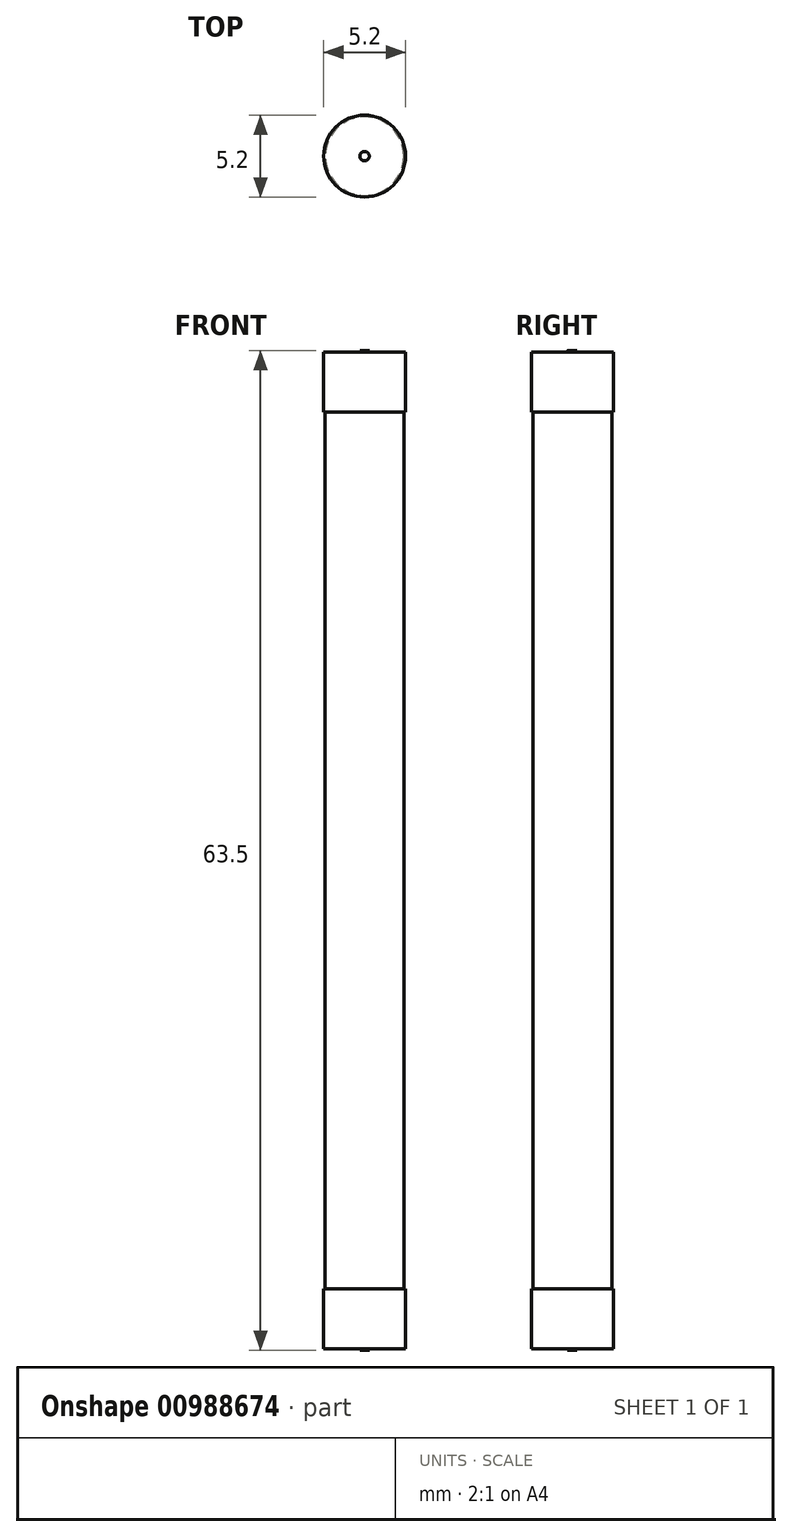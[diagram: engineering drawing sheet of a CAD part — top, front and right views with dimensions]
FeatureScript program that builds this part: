
annotation { "Feature Type Name" : "Feature", "Feature Type Description" : "" }
export const myFeature = defineFeature(function(context is Context, id is Id, definition is map)
    precondition{}
    {
        {
            var Q0;
            Q0=qCreatedBy(makeId("Top.planeOp"),FACE);
            var sketch = newSketch(context, id + "F0", { "sketchPlane" : qUnion([Q0])});
            skCircle(sketch, "E0", {"center": v(0, 0) * mm, "radius": 2.5 * mm});
            skSolve(sketch);
        }
        {
            var Q0;
            Q0=makeQuery(id+"F0.imprint","IMPRINT",FACE,{"disambiguationData":[TD([[makeQuery(id+"F0.imprint","IMPRINT",EDGE,{"derivedFrom":sQuery(id+"F0.wireOp",EDGE,"E0")}),1.0]])]});
            extrude(context, id + "F1", {"entities" : qUnion([Q0]), "endBound" : BoundingType.SYMMETRIC, "depth" : 55.67 * mm, "offsetDistance" : 25 * mm});
        }
        {
            var Q0;
            Q0=makeQuery(id+"F1.opExtrude","CAP_FACE",FACE,{"disambiguationData":[OSD([sQuery(id+"F0.wireOp",EDGE,"E0")])],"isStart":false});
            var sketch = newSketch(context, id + "F2", { "sketchPlane" : qUnion([Q0])});
            skCircle(sketch, "E1", {"center": v(0, 0) * mm, "radius": 2.6 * mm});
            skSolve(sketch);
        }
        {
            var Q0;
            Q0=makeQuery(id+"F2.imprint","IMPRINT",FACE,{"disambiguationData":[TD([[makeQuery(id+"F2.imprint","IMPRINT",EDGE,{"derivedFrom":makeQuery(id+"F1.opExtrude","CAP_EDGE",EDGE,{"disambiguationData":[OSD([sQuery(id+"F0.wireOp",EDGE,"E0")])],"isStart":false})}),1.0]])]});
            var Q1;
            Q1=makeQuery(id+"F2.imprint","IMPRINT",FACE,{"disambiguationData":[TD([[makeQuery(id+"F2.imprint","IMPRINT",EDGE,{"derivedFrom":sQuery(id+"F2.wireOp",EDGE,"E1")}),1.0]])]});
            extrude(context, id + "F3", {"entities" : qUnion([Q0, Q1]), "operationType" : NewBodyOperationType.ADD, "depth" : 3.81 * mm, "offsetDistance" : 25 * mm});
        }
        {
            var Q0;
            Q0=makeQuery(id+"F1.opExtrude","CAP_FACE",FACE,{"disambiguationData":[OSD([sQuery(id+"F0.wireOp",EDGE,"E0")])],"isStart":true});
            var sketch = newSketch(context, id + "F4", { "sketchPlane" : qUnion([Q0])});
            skCircle(sketch, "E2", {"center": v(0, 0) * mm, "radius": 2.6 * mm});
            skSolve(sketch);
        }
        {
            var Q0;
            Q0=makeQuery(id+"F4.imprint","IMPRINT",FACE,{"disambiguationData":[TD([[makeQuery(id+"F4.imprint","IMPRINT",EDGE,{"derivedFrom":makeQuery(id+"F1.opExtrude","CAP_EDGE",EDGE,{"disambiguationData":[OSD([sQuery(id+"F0.wireOp",EDGE,"E0")])],"isStart":true})}),-1.0]])]});
            var Q1;
            Q1=makeQuery(id+"F4.imprint","IMPRINT",FACE,{"disambiguationData":[TD([[makeQuery(id+"F4.imprint","IMPRINT",EDGE,{"derivedFrom":sQuery(id+"F4.wireOp",EDGE,"E2")}),1.0]])]});
            extrude(context, id + "F5", {"entities" : qUnion([Q0, Q1]), "operationType" : NewBodyOperationType.ADD, "depth" : 3.81 * mm, "offsetDistance" : 25 * mm});
        }
        {
            var Q0;
            Q0=makeQuery(id+"F5.opExtrude","CAP_FACE",FACE,{"disambiguationData":[OSD([sQuery(id+"F4.wireOp",EDGE,"E2")])],"isStart":false});
            var sketch = newSketch(context, id + "F6", { "sketchPlane" : qUnion([Q0])});
            skCircle(sketch, "E3", {"center": v(0, 0) * mm, "radius": 0.3 * mm});
            skSolve(sketch);
        }
        {
            var Q0;
            Q0=makeQuery(id+"F6.imprint","IMPRINT",FACE,{"disambiguationData":[TD([[makeQuery(id+"F6.imprint","IMPRINT",EDGE,{"derivedFrom":sQuery(id+"F6.wireOp",EDGE,"E3")}),1.0]])]});
            extrude(context, id + "F7", {"entities" : qUnion([Q0]), "operationType" : NewBodyOperationType.ADD, "depth" : 0.1 * mm, "offsetDistance" : 25 * mm});
        }
        {
            var Q0;
            Q0=makeQuery(id+"F3.opExtrude","CAP_FACE",FACE,{"disambiguationData":[OSD([sQuery(id+"F2.wireOp",EDGE,"E1")])],"isStart":false});
            var sketch = newSketch(context, id + "F8", { "sketchPlane" : qUnion([Q0])});
            skCircle(sketch, "E4", {"center": v(0, 0) * mm, "radius": 0.3 * mm});
            skSolve(sketch);
        }
        {
            var Q0;
            Q0=makeQuery(id+"F8.imprint","IMPRINT",FACE,{"disambiguationData":[TD([[makeQuery(id+"F8.imprint","IMPRINT",EDGE,{"derivedFrom":sQuery(id+"F8.wireOp",EDGE,"E4")}),1.0]])]});
            extrude(context, id + "F9", {"entities" : qUnion([Q0]), "operationType" : NewBodyOperationType.ADD, "depth" : 0.1 * mm, "offsetDistance" : 25 * mm});
        }
    });
